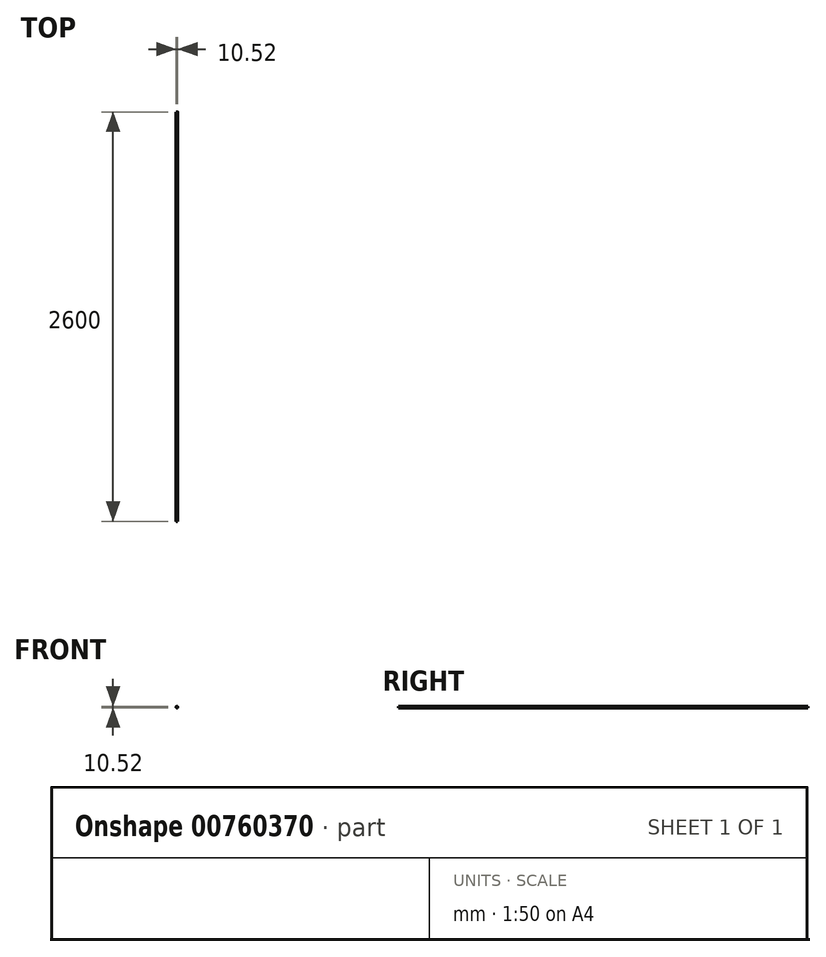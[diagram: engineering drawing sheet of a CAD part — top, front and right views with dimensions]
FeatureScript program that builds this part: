
annotation { "Feature Type Name" : "Feature", "Feature Type Description" : "" }
export const myFeature = defineFeature(function(context is Context, id is Id, definition is map)
    precondition{}
    {
        {
            assignVariable(context, id + "F0", {"name" : "LENGTH", "anyValue" : 2600});
        }
        {
            var Q0;
            Q0=qCreatedBy(makeId("Front.planeOp"),FACE);
            var sketch = newSketch(context, id + "F1", { "sketchPlane" : qUnion([Q0])});
            skCircle(sketch, "E0", {"center": v(0, 0) * mm, "radius": 5.26 * mm});
            skSolve(sketch);
        }
        {
            var Q0;
            Q0=makeQuery(id+"F1.imprint","IMPRINT",FACE,{"disambiguationData":[TD([[makeQuery(id+"F1.imprint","IMPRINT",EDGE,{"derivedFrom":sQuery(id+"F1.wireOp",EDGE,"E0")}),1.0]])]});
            extrude(context, id + "F2", {"entities" : qUnion([Q0]), "oppositeDirection" : true, "depth" : (getVariable(context, 'LENGTH')) * mm, "offsetDistance" : 25 * mm});
        }
    });
